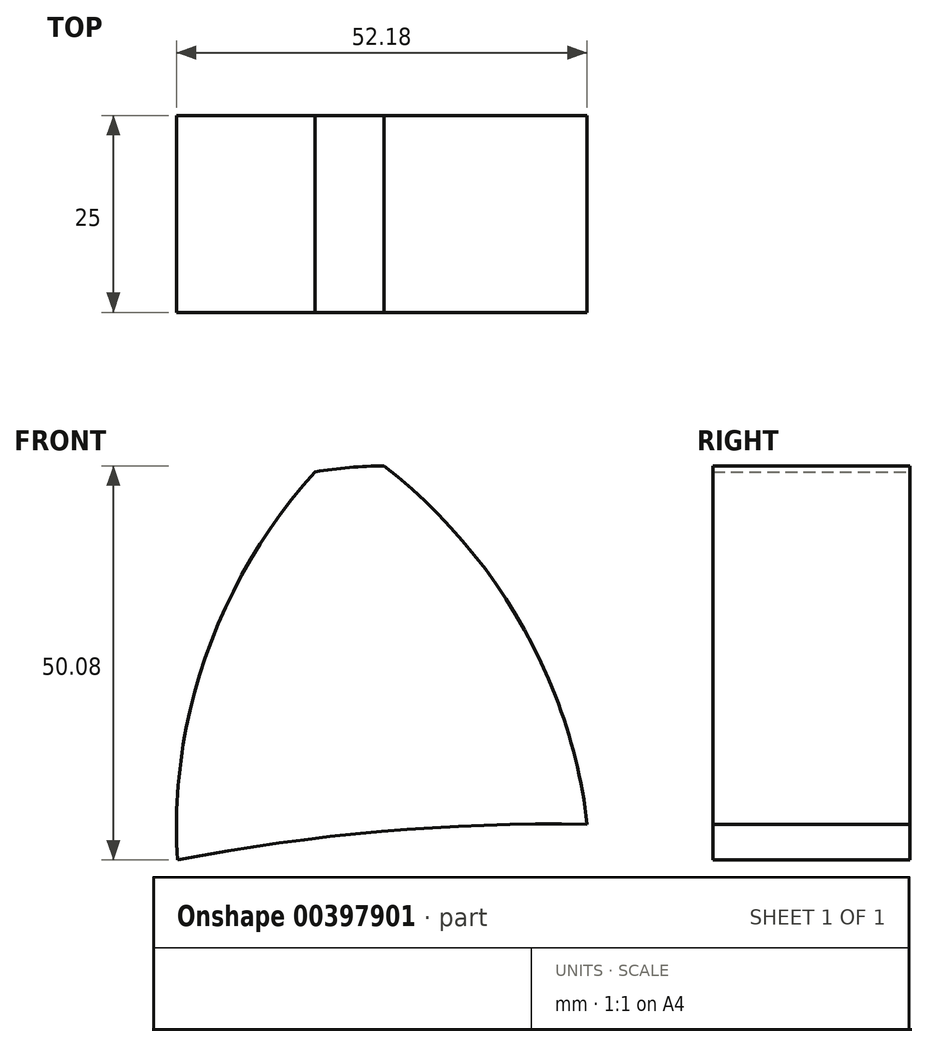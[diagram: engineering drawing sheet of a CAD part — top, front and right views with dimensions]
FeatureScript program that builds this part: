
annotation { "Feature Type Name" : "Feature", "Feature Type Description" : "" }
export const myFeature = defineFeature(function(context is Context, id is Id, definition is map)
    precondition{}
    {
        {
            var Q0;
            Q0=qCreatedBy(makeId("Front.planeOp"),FACE);
            var sketch = newSketch(context, id + "F0", { "sketchPlane" : qUnion([Q0])});
            skCircle(sketch, "E0", {"center": v(0, 0) * mm, "radius": 300 * mm, "construction": true});
            skCircle(sketch, "E1", {"center": v(0, 0) * mm, "radius": 270 * mm, "construction": true});
            skCircle(sketch, "E2", {"center": v(0, 0) * mm, "radius": 253.5 * mm, "construction": true});
            skLineSegment(sketch, "E3", {"start": v(0, 0) * mm, "end": v(0, 414.93) * mm, "construction": true});
            skLineSegment(sketch, "E4", {"start": v(0, 0) * mm, "end": v(-36.4, 416.1) * mm, "construction": true});
            skLineSegment(sketch, "E5", {"start": v(0, 270) * mm, "end": v(-427.1, 270) * mm, "construction": true});
            skLineSegment(sketch, "E6", {"start": v(0, 270) * mm, "end": v(-407.51, 121.68) * mm, "construction": true});
            skCircle(sketch, "E7", {"center": v(0, 270) * mm, "radius": 67.5 * mm, "construction": true});
            skCircle(sketch, "E8", {"center": v(0, 0) * mm, "radius": 253.72 * mm});
            skCircle(sketch, "E9", {"center": v(-63, 245.77) * mm, "radius": 67.5 * mm, "construction": true});
            skArc(sketch, "E10", {"start": v(0, 270) * mm, "mid": v(-8.9, 286.08) * mm, "end": v(-21.76, 299.2) * mm});
            skArc(sketch, "E11", {"start": v(4.06, 253.47) * mm, "mid": v(2.57, 261.87) * mm, "end": v(0, 270) * mm});
            skArc(sketch, "E12.MirrorCS", {"start": v(-46.89, 265.9) * mm, "mid": v(-40.9, 283.28) * mm, "end": v(-30.52, 298.44) * mm});
            skArc(sketch, "E13.MirrorCS", {"start": v(-48.01, 248.91) * mm, "mid": v(-48, 257.44) * mm, "end": v(-46.89, 265.9) * mm});
            skArc(sketch, "E14", {"start": v(-21.76, 299.2) * mm, "mid": v(-26.16, 299) * mm, "end": v(-30.52, 298.44) * mm});
            skSolve(sketch);
        }
        {
            var Q0;
            {var subQ2=sQuery(id+"F0.wireOp",EDGE,"E10");Q0=makeQuery(id+"F0.imprint","IMPRINT",FACE,{"disambiguationData":[TD([[makeQuery(id+"F0.imprint","IMPRINT",EDGE,{"derivedFrom":subQ2}),1.0]])]});}
            extrude(context, id + "F1", {"entities" : qUnion([Q0]), "depth" : 25 * mm});
        }
    });
